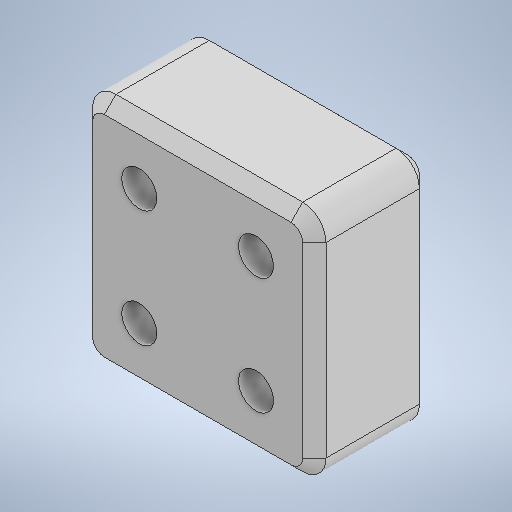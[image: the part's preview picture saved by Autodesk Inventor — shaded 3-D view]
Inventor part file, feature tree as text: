
AUTODESK INVENTOR PART (.ipt)
format: ipt  version: 2025.3 (Build 293356000, 356)  size: 547,328 bytes
history: native  units: mm
features: other x1, extrude x1, fillet x1, chamfer x1, sketch x1
ambient origin geometry x8: Origin, YZ Plane, XZ Plane, XY Plane, X Axis, Y Axis, Z Axis, Center Point
bodies: Body1 (feature_tree)
feature tree (5):
  other  "솔리드1"
  extrude  "돌출1"  Depth=20.0mm
  fillet  "모깎기1"  Radius=5.0mm
  chamfer  "모따기1"  Distance=3.0mm
  sketch  "스케치1"
